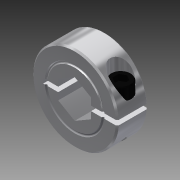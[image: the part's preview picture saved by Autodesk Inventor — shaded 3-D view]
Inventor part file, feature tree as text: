
AUTODESK INVENTOR PART (.ipt)
format: ipt  version: 2014 (Build 180170000, 170)  size: 260,608 bytes
history: native  units: in
note: dims shown in document units (in); Inventor stores cm internally (conversion verified against a paired STEP export)
features: extrude x2, sketch x2, other x1, imported_body x1
ambient origin geometry x8: Origin, YZ Plane, XZ Plane, XY Plane, X Axis, Y Axis, Z Axis, Center Point
bodies: Solid1 (feature_tree)
feature tree (6):
  other  "CL-8-A1"
  extrude  "Extrusion1"  Depth=0.4375in TaperAngle=0.0deg
  extrude  "Extrusion2"  [1 undecoded]
  imported_body  "Base1"
  sketch  "Sketch2"  dims[d0=0.5in d1=0.4375in d2=0.0in]
  sketch  "Sketch3"  dims[d3=1.0in d4=0.0in]
note: 1 required parameter value undecoded (feature->parameter linkage not recoverable at this tier; creation-order binding heuristic only, values carry confidence <= 0.55)
